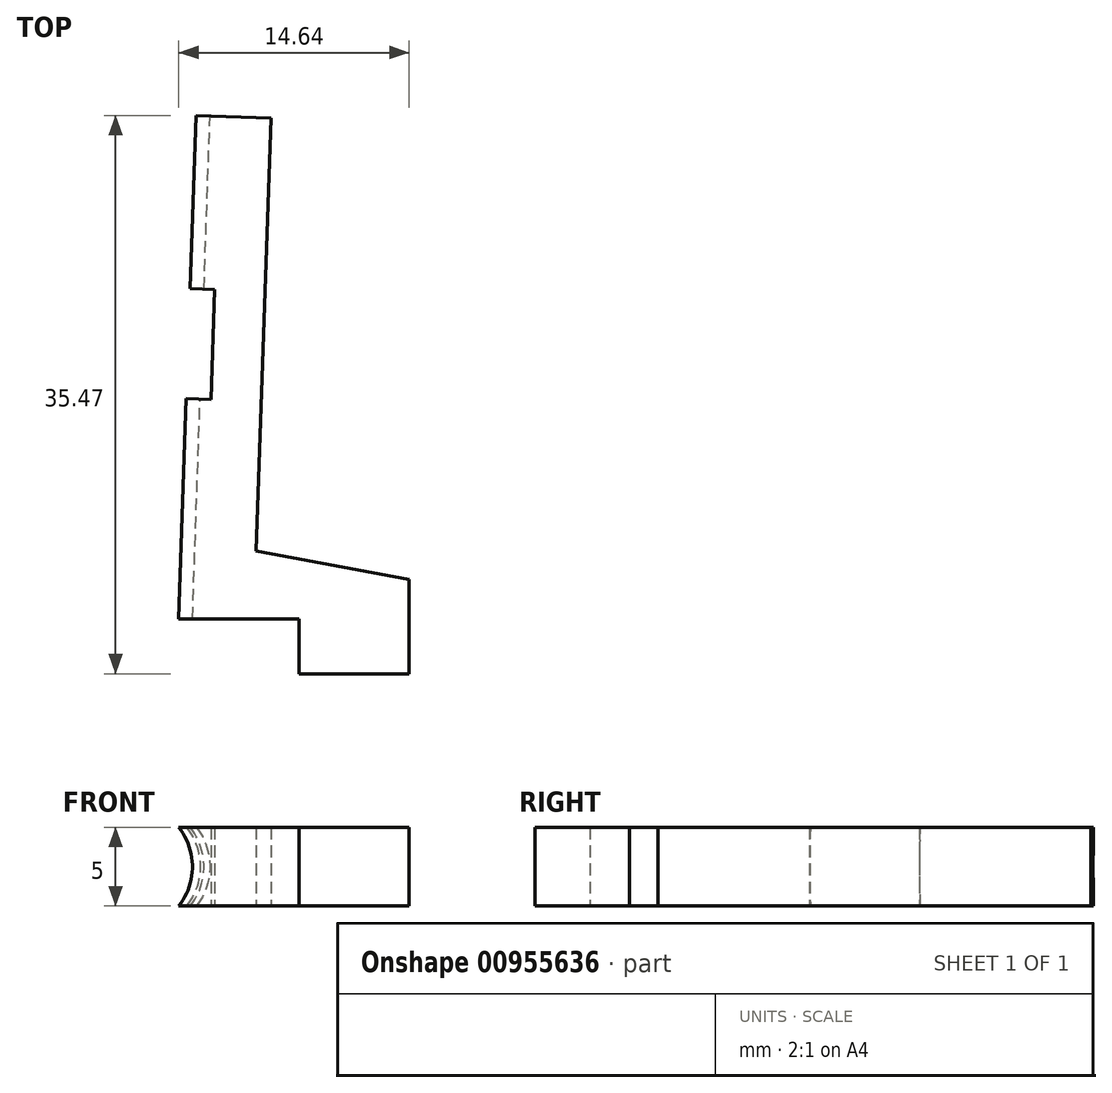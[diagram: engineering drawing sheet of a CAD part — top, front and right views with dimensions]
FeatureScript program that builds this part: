
annotation { "Feature Type Name" : "Feature", "Feature Type Description" : "" }
export const myFeature = defineFeature(function(context is Context, id is Id, definition is map)
    precondition{}
    {
        {
            var Q0;
            Q0=qCreatedBy(makeId("Top.planeOp"),FACE);
            var sketch = newSketch(context, id + "F0", { "sketchPlane" : qUnion([Q0])});
            skLineSegment(sketch, "E0", {"start": v(-0.02, -0.5) * mm, "end": v(0, 0) * mm});
            skLineSegment(sketch, "E1", {"start": v(0, 0) * mm, "end": v(8, 0) * mm, "construction": true});
            skLineSegment(sketch, "E2", {"start": v(8, 0) * mm, "end": v(8, 3.5) * mm, "construction": true});
            skLineSegment(sketch, "E3", {"start": v(8, 0) * mm, "end": v(15, 0) * mm});
            skLineSegment(sketch, "E4", {"start": v(15, 0) * mm, "end": v(15, 6) * mm});
            skLineSegment(sketch, "E5", {"start": v(-0.02, -0.5) * mm, "end": v(0, 0) * mm, "construction": true});
            skLineSegment(sketch, "E6", {"start": v(0.61, 17.49) * mm, "end": v(2.4, 17.43) * mm, "construction": true});
            skLineSegment(sketch, "E7", {"start": v(2.4, 17.43) * mm, "end": v(2.65, 24.42) * mm, "construction": true});
            skLineSegment(sketch, "E8", {"start": v(2.65, 24.42) * mm, "end": v(0.61, 24.5) * mm, "construction": true});
            skLineSegment(sketch, "E9", {"start": v(0.61, 17.49) * mm, "end": v(2.4, 17.43) * mm});
            skLineSegment(sketch, "E10", {"start": v(2.65, 24.42) * mm, "end": v(0.86, 24.49) * mm});
            skLineSegment(sketch, "E11", {"start": v(1.24, 35.48) * mm, "end": v(6.24, 35.3) * mm});
            skLineSegment(sketch, "E12", {"start": v(6.24, 35.3) * mm, "end": v(5.28, 7.8) * mm});
            skLineSegment(sketch, "E13", {"start": v(5.28, 7.8) * mm, "end": v(15, 6) * mm});
            skLineSegment(sketch, "E14", {"start": v(8, 0) * mm, "end": v(8, 3.5) * mm});
            skLineSegment(sketch, "E15", {"start": v(0.12, 3.5) * mm, "end": v(8, 3.5) * mm});
            skLineSegment(sketch, "E16.trimOffspring", {"start": v(0.86, 24.49) * mm, "end": v(1.24, 35.48) * mm});
            skLineSegment(sketch, "E17", {"start": v(2.65, 24.42) * mm, "end": v(2.4, 17.43) * mm});
            skLineSegment(sketch, "E18.trimOffspring", {"start": v(0.12, 3.5) * mm, "end": v(0.61, 17.49) * mm, "construction": true});
            skLineSegment(sketch, "E19.trimOffspring", {"start": v(0.12, 3.5) * mm, "end": v(0.61, 17.49) * mm});
            skSolve(sketch);
        }
        {
            var Q0;
            Q0 = qSketchRegion(id + "F0", true);
            extrude(context, id + "F1", {"entities" : qUnion([Q0]), "depth" : 5 * mm, "offsetDistance" : 25 * mm, "symmetric" : true});
        }
        {
            var Q0;
            Q0=makeQuery(id+"F1.opExtrude","SWEPT_FACE",FACE,{"disambiguationData":[OSD([sQuery(id+"F0.wireOp",EDGE,"E11")])]});
            var sketch = newSketch(context, id + "F2", { "sketchPlane" : qUnion([Q0])});
            skCircle(sketch, "E20", {"center": v(2.89, 0) * mm, "radius": 4 * mm});
            skSolve(sketch);
        }
        {
            var Q0;
            Q0 = qSketchRegion(id + "F2", true);
            extrude(context, id + "F3", {"entities" : qUnion([Q0]), "operationType" : NewBodyOperationType.REMOVE, "oppositeDirection" : true, "depth" : 40 * mm, "offsetDistance" : 25 * mm});
        }
    });
